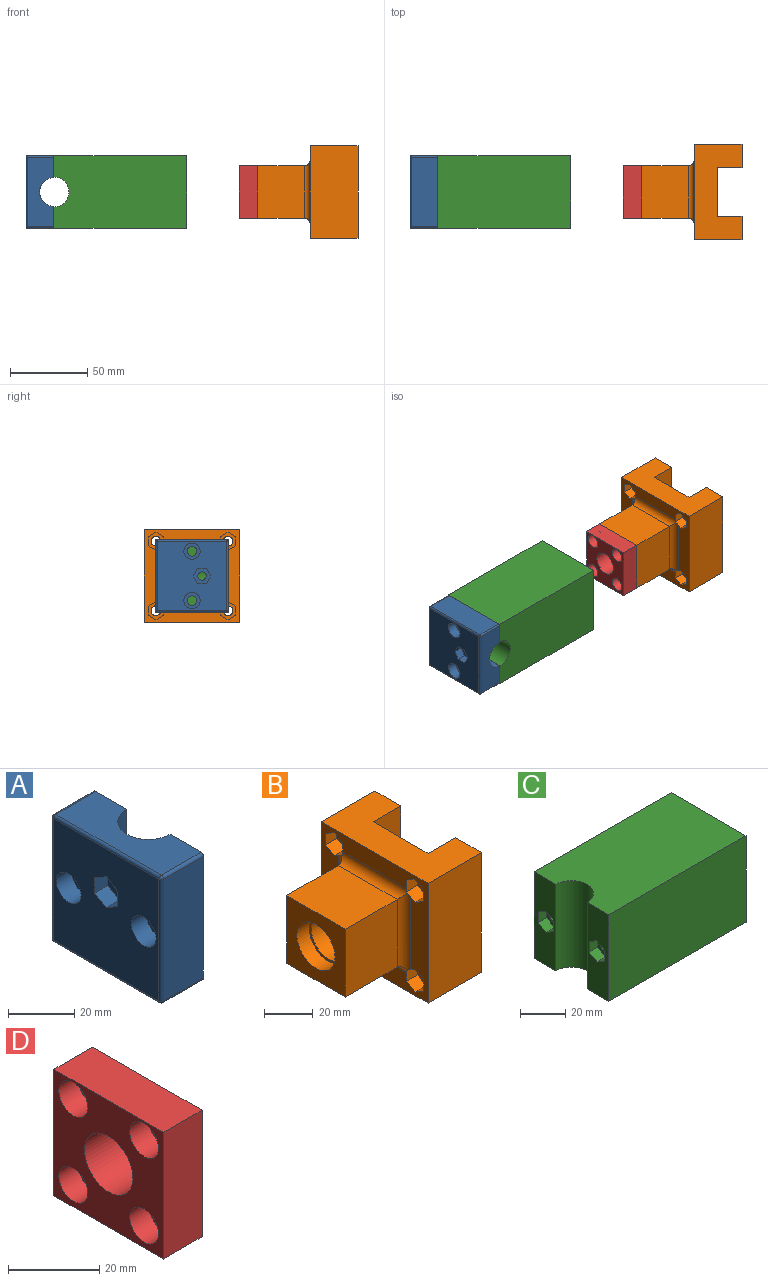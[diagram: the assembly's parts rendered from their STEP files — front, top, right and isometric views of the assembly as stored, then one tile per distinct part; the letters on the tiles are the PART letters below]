
ASSEMBLY  parts=4 mates=9
PART A: 34 faces, bbox 18x47x47 mm
  f0: cylinder r=2.7mm len=5.4mm, axis (-1,0,0), area 57.7mm2, adj f13,f33
  f1: plane 47x14.25mm, normal (1,0,0), area 639.1mm2, adj f7,f10,f11,f12,f13,f16,f22
  f2: cylinder r=5.25mm len=10.5mm, axis (-1,0,0), area 214.4mm2, adj f3,f8
  f3: plane 10.5x10.5mm, normal (-1,0,0), area 56.4mm2, adj f2,f4
  f4: cylinder r=3.1mm len=11.5mm, axis (-1,0,0), area 224mm2, adj f3,f14
  f5: cylinder r=5.25mm len=10.5mm, axis (-1,0,0), area 214.4mm2, adj f6,f8
  f6: plane 10.5x10.5mm, normal (-1,0,0), area 56.4mm2, adj f5,f7
  f7: cylinder r=3.1mm len=11.5mm, axis (-1,0,0), area 224mm2, adj f1,f6
  f8: plane 45x45mm, normal (-1,0,0), area 1766.9mm2, adj f2,f5,f17,f20,f23,f26,f27,f28
  f9: plane 45x17mm, normal (0,1,0), area 765mm2, adj f14,f15,f20,f21
  f10: plane 45x17mm, normal (0,-1,0), area 765mm2, adj f1,f16,f22,f23
  f11: plane 45x17mm, normal (0,0,-1), area 630.6mm2, adj f1,f13,f14,f15,f16,f17
  f12: plane 45x17mm, normal (0,0,1), area 630.6mm2, adj f1,f13,f14,f21,f22,f26
  f13: cylinder r=9.25mm len=47mm, axis (0,0,1), area 1342.7mm2, adj f0,f1,f11,f12,f14
  f14: plane 47x14.25mm, normal (1,0,0), area 639.1mm2, adj f4,f9,f11,f12,f13,f15,f21
  f15: cylinder r=1mm len=17mm, axis (1,0,0), area 26.7mm2, adj f9,f11,f14,f18
  f16: cylinder r=1mm len=17mm, axis (-1,0,0), area 26.7mm2, adj f1,f10,f11,f19
  f17: cylinder r=1mm len=45mm, axis (0,-1,0), area 70.7mm2, adj f8,f11,f18,f19
  f18: sphere r=1mm, area 1.6mm2, adj f15,f17,f20
  f19: sphere r=1mm, area 1.6mm2, adj f16,f17,f23
  f20: cylinder r=1mm len=45mm, axis (0,0,1), area 70.7mm2, adj f8,f9,f18,f24
  f21: cylinder r=1mm len=17mm, axis (-1,0,0), area 26.7mm2, adj f9,f12,f14,f24
  f22: cylinder r=1mm len=17mm, axis (1,0,0), area 26.7mm2, adj f1,f10,f12,f25
  f23: cylinder r=1mm len=45mm, axis (0,0,-1), area 70.7mm2, adj f8,f10,f19,f25
  f24: sphere r=1mm, area 1.6mm2, adj f20,f21,f26
  f25: sphere r=1mm, area 1.6mm2, adj f22,f23,f26
  f26: cylinder r=1mm len=45mm, axis (0,1,0), area 70.7mm2, adj f8,f12,f24,f25
  f27: plane 5.55x4.95mm, normal (0,-0.5,-0.87), area 31.7mm2, adj f8,f28,f32,f33
  f28: plane 5.72x5.55mm, normal (0,-1,0), area 31.7mm2, adj f8,f27,f29,f33
  f29: plane 5.55x4.95mm, normal (0,-0.5,0.87), area 31.7mm2, adj f8,f28,f30,f33
  f30: plane 5.55x4.95mm, normal (0,0.5,0.87), area 31.7mm2, adj f8,f29,f31,f33
  f31: plane 5.72x5.55mm, normal (0,1,0), area 31.7mm2, adj f8,f30,f32,f33
  f32: plane 5.55x4.95mm, normal (0,0.5,-0.87), area 31.7mm2, adj f8,f27,f31,f33
  f33: plane 11.43x9.9mm, normal (-1,0,0), area 62mm2, adj f0,f27,f28,f29,f30,f31,f32
PART B: 55 faces, bbox 64.9x61.8x60 mm
  f0: plane 61.75x60mm, normal (-1,0,0), area 1617.1mm2, adj f5,f6,f7,f8,f15,f16,f17,f18
  f1: plane 60x15mm, normal (1,0,0), area 837.7mm2, adj f3,f5,f6,f8,f9,f11
  f2: plane 60x15mm, normal (1,0,0), area 837.7mm2, adj f4,f5,f6,f7,f10,f12
  f3: cylinder r=3.15mm len=24.38mm, axis (1,0,0), area 482.4mm2, adj f1,f28
  f4: cylinder r=3.15mm len=24.38mm, axis (1,0,0), area 482.4mm2, adj f2,f14
  f5: plane 61.75x30.88mm, normal (0,0,1), area 1402.5mm2, adj f0,f1,f2,f7,f8,f9,f10,f13
  f6: plane 61.75x30.88mm, normal (0,0,-1), area 1402.5mm2, adj f0,f1,f2,f7,f8,f9,f10,f13
  f7: plane 60x30.88mm, normal (0,1,0), area 1852.5mm2, adj f0,f2,f5,f6
  f8: plane 60x30.88mm, normal (0,-1,0), area 1852.5mm2, adj f0,f1,f5,f6
  f9: plane 60x15.88mm, normal (0,1,0), area 952.5mm2, adj f1,f5,f6,f13
  f10: plane 60x15.88mm, normal (0,-1,0), area 952.5mm2, adj f2,f5,f6,f13
  f11: cylinder r=3.15mm len=24.38mm, axis (1,0,0), area 482.4mm2, adj f1,f21
  f12: cylinder r=3.15mm len=24.38mm, axis (1,0,0), area 482.4mm2, adj f2,f35
  f13: plane 60x31.75mm, normal (1,0,0), area 1905mm2, adj f5,f6,f9,f10
  f14: plane 11.55x10mm, normal (-1,0,0), area 55.4mm2, adj f4,f15,f16,f17,f18,f19,f20
  f15: plane 6.5x5mm, normal (0,-0.5,-0.87), area 37.5mm2, adj f0,f14,f16,f20
  f16: plane 6.5x5mm, normal (0,0.5,-0.87), area 37.5mm2, adj f0,f14,f15,f17
  f17: plane 6.75x5.77mm, normal (0,1,0), area 37.6mm2, adj f0,f14,f16,f18,f48
  f18: plane 6.96x5.01mm, normal (0,0.5,0.87), area 38.1mm2, adj f0,f14,f17,f19,f48,f50
  f19: plane 6.5x5mm, normal (0,-0.5,0.87), area 37.5mm2, adj f0,f14,f18,f20
  f20: plane 6.5x5.77mm, normal (0,-1,0), area 37.5mm2, adj f0,f14,f15,f19
  f21: plane 11.55x10mm, normal (-1,0,0), area 55.4mm2, adj f11,f22,f23,f24,f25,f26,f27
  f22: plane 6.5x5mm, normal (0,-0.5,-0.87), area 37.5mm2, adj f0,f21,f23,f27
  f23: plane 6.5x5mm, normal (0,0.5,-0.87), area 37.5mm2, adj f0,f21,f22,f24
  f24: plane 6.5x5.77mm, normal (0,1,0), area 37.5mm2, adj f0,f21,f23,f25
  f25: plane 6.5x5mm, normal (0,0.5,0.87), area 37.5mm2, adj f0,f21,f24,f26
  f26: plane 6.96x5.01mm, normal (0,-0.5,0.87), area 38.1mm2, adj f0,f21,f25,f27,f47,f48
  f27: plane 6.75x5.77mm, normal (0,-1,0), area 37.6mm2, adj f0,f21,f22,f26,f48
  f28: plane 11.55x10mm, normal (-1,0,0), area 55.4mm2, adj f3,f29,f30,f31,f32,f33,f34
  f29: plane 6.5x5mm, normal (0,0.5,0.87), area 37.5mm2, adj f0,f28,f30,f34
  f30: plane 6.5x5mm, normal (0,-0.5,0.87), area 37.5mm2, adj f0,f28,f29,f31
  f31: plane 6.75x5.77mm, normal (0,-1,0), area 37.6mm2, adj f0,f28,f30,f32,f49
  f32: plane 6.96x5.01mm, normal (0,-0.5,-0.87), area 38.1mm2, adj f0,f28,f31,f33,f47,f49
  f33: plane 6.5x5mm, normal (0,0.5,-0.87), area 37.5mm2, adj f0,f28,f32,f34
  f34: plane 6.5x5.77mm, normal (0,1,0), area 37.5mm2, adj f0,f28,f29,f33
  f35: plane 11.55x10mm, normal (-1,0,0), area 55.4mm2, adj f12,f36,f37,f38,f39,f40,f41
  f36: plane 6.5x5mm, normal (0,0.5,0.87), area 37.5mm2, adj f0,f35,f37,f41
  f37: plane 6.5x5mm, normal (0,-0.5,0.87), area 37.5mm2, adj f0,f35,f36,f38
  f38: plane 6.5x5.77mm, normal (0,-1,0), area 37.5mm2, adj f0,f35,f37,f39
  f39: plane 6.5x5mm, normal (0,-0.5,-0.87), area 37.5mm2, adj f0,f35,f38,f40
  f40: plane 6.96x5.01mm, normal (0,0.5,-0.87), area 38.1mm2, adj f0,f35,f39,f41,f49,f50
  f41: plane 6.75x5.77mm, normal (0,1,0), area 37.6mm2, adj f0,f35,f36,f40,f49
  f42: plane 34x30mm, normal (0,1,0), area 1020mm2, adj f43,f45,f46,f50
  f43: plane 34x30mm, normal (0,0,-1), area 1020mm2, adj f42,f44,f46,f49
  f44: plane 34x30mm, normal (0,-1,0), area 1020mm2, adj f43,f45,f46,f47
  f45: plane 34x30mm, normal (0,0,1), area 1020mm2, adj f42,f44,f46,f48
  f46: plane 34x34mm, normal (-1,0,0), area 774.1mm2, adj f42,f43,f44,f45,f52
  f47: cylinder r=4mm len=38.32mm, axis (0,0,-1), area 226.5mm2, adj f0,f26,f32,f44,f48,f49
  f48: cylinder r=4mm len=38.32mm, axis (0,-1,0), area 225.8mm2, adj f0,f17,f18,f26,f27,f45,f47,f50
  f49: cylinder r=4mm len=38.32mm, axis (0,1,0), area 225.8mm2, adj f0,f31,f32,f40,f41,f43,f47,f50
  f50: cylinder r=4mm len=38.32mm, axis (0,0,1), area 226.5mm2, adj f0,f18,f40,f42,f48,f49
  f51: plane 22.05x22.05mm, normal (-1,0,0), area 77.1mm2, adj f52,f54
  f52: cylinder r=11.03mm len=22.05mm, axis (-1,0,0), area 491.8mm2, adj f46,f51
  f53: plane 19.7x19.7mm, normal (-1,0,0), area 304.8mm2, adj f54
  f54: cylinder r=9.85mm len=22.9mm, axis (-1,0,0), area 1417.3mm2, adj f51,f53
PART C: 33 faces, bbox 86x47x47 mm
  f0: plane 47x13.75mm, normal (-1,0,0), area 561.4mm2, adj f12,f13,f14,f15,f26,f27,f28,f29
  f1: plane 47x13.75mm, normal (-1,0,0), area 561.4mm2, adj f4,f5,f6,f7,f9,f10,f11,f12
  f2: plane 6.2x6.2mm, normal (-1,0,0), area 30.2mm2, adj f3
  f3: cylinder r=3.1mm len=7.72mm, axis (-1,0,0), area 150.4mm2, adj f2,f8
  f4: plane 5.3x4.95mm, normal (0,0.5,-0.87), area 30.3mm2, adj f1,f5,f7,f8
  f5: plane 5.72x5.3mm, normal (0,1,0), area 30.3mm2, adj f1,f4,f6,f8
  f6: plane 5.3x4.95mm, normal (0,0.5,0.87), area 30.3mm2, adj f1,f5,f8,f9
  f7: plane 5.3x4.95mm, normal (0,-0.5,-0.87), area 30.3mm2, adj f1,f4,f8,f10
  f8: plane 11.43x9.9mm, normal (-1,0,0), area 54.7mm2, adj f3,f4,f5,f6,f7,f9,f10
  f9: plane 5.3x4.95mm, normal (0,-0.5,0.87), area 30.3mm2, adj f1,f6,f8,f10
  f10: plane 5.72x5.3mm, normal (0,-1,0), area 30.3mm2, adj f1,f7,f8,f9
  f11: plane 86x47mm, normal (0,1,0), area 4042mm2, adj f1,f12,f14,f16
  f12: plane 86x47mm, normal (0,0,-1), area 3892.7mm2, adj f0,f1,f11,f13,f15,f16
  f13: plane 86x47mm, normal (0,-1,0), area 4042mm2, adj f0,f12,f14,f16
  f14: plane 86x47mm, normal (0,0,1), area 3892.7mm2, adj f0,f1,f11,f13,f15,f16
  f15: cylinder r=9.75mm len=47mm, axis (0,0,1), area 1439.6mm2, adj f0,f1,f12,f14
  f16: plane 47x47mm, normal (1,0,0), area 1011.8mm2, adj f11,f12,f13,f14,f17,f18,f19,f20
  f17: plane 34.6x28mm, normal (0,1,0), area 968.8mm2, adj f16,f18,f20,f23
  f18: plane 34.6x28mm, normal (0,0,-1), area 968.8mm2, adj f16,f17,f19,f23
  f19: plane 34.6x28mm, normal (0,-1,0), area 968.8mm2, adj f16,f18,f20,f23
  f20: plane 34.6x28mm, normal (0,0,1), area 968.8mm2, adj f16,f17,f19,f23
  f21: plane 8x8mm, normal (1,0,0), area 50.3mm2, adj f22
  f22: cylinder r=4mm len=20mm, axis (1,0,0), area 502.7mm2, adj f21,f23
  f23: plane 34.6x34.6mm, normal (1,0,0), area 1146.9mm2, adj f17,f18,f19,f20,f22
  f24: plane 6.2x6.2mm, normal (-1,0,0), area 30.2mm2, adj f25
  f25: cylinder r=3.1mm len=7.72mm, axis (-1,0,0), area 150.4mm2, adj f24,f30
  f26: plane 5.3x4.95mm, normal (0,-0.5,-0.87), area 30.3mm2, adj f0,f27,f29,f30
  f27: plane 5.3x4.95mm, normal (0,0.5,-0.87), area 30.3mm2, adj f0,f26,f28,f30
  f28: plane 5.72x5.3mm, normal (0,1,0), area 30.3mm2, adj f0,f27,f30,f31
  f29: plane 5.72x5.3mm, normal (0,-1,0), area 30.3mm2, adj f0,f26,f30,f32
  f30: plane 11.43x9.9mm, normal (-1,0,0), area 54.7mm2, adj f25,f26,f27,f28,f29,f31,f32
  f31: plane 5.3x4.95mm, normal (0,0.5,0.87), area 30.3mm2, adj f0,f28,f30,f32
  f32: plane 5.3x4.95mm, normal (0,-0.5,0.87), area 30.3mm2, adj f0,f29,f30,f31
PART D: 19 faces, bbox 12x34x34 mm
  f0: cylinder r=2.6mm len=6mm, axis (1,0,0), area 98mm2, adj f10,f18
  f1: cylinder r=2.6mm len=6mm, axis (1,0,0), area 98mm2, adj f10,f16
  f2: cylinder r=2.6mm len=6mm, axis (1,0,0), area 98mm2, adj f10,f14
  f3: cylinder r=2.6mm len=6mm, axis (1,0,0), area 98mm2, adj f10,f12
  f4: plane 34x12mm, normal (0,0,1), area 408mm2, adj f5,f8,f9,f10
  f5: plane 34x12mm, normal (0,1,0), area 408mm2, adj f4,f6,f9,f10
  f6: plane 34x12mm, normal (0,0,-1), area 408mm2, adj f5,f8,f9,f10
  f7: cylinder r=7.5mm len=15mm, axis (1,0,0), area 565.5mm2, adj f9,f10
  f8: plane 34x12mm, normal (0,-1,0), area 408mm2, adj f4,f6,f9,f10
  f9: plane 34x34mm, normal (-1,0,0), area 730.4mm2, adj f4,f5,f6,f7,f8,f11,f13,f15
  f10: plane 34x34mm, normal (1,0,0), area 894.3mm2, adj f0,f1,f2,f3,f4,f5,f6,f7
  f11: cylinder r=4.45mm len=8.9mm, axis (-1,0,0), area 167.8mm2, adj f9,f12
  f12: plane 8.9x8.9mm, normal (-1,0,0), area 41mm2, adj f3,f11
  f13: cylinder r=4.45mm len=8.9mm, axis (-1,0,0), area 167.8mm2, adj f9,f14
  f14: plane 8.9x8.9mm, normal (-1,0,0), area 41mm2, adj f2,f13
  f15: cylinder r=4.45mm len=8.9mm, axis (-1,0,0), area 167.8mm2, adj f9,f16
  f16: plane 8.9x8.9mm, normal (-1,0,0), area 41mm2, adj f1,f15
  f17: cylinder r=4.45mm len=8.9mm, axis (-1,0,0), area 167.8mm2, adj f9,f18
  f18: plane 8.9x8.9mm, normal (-1,0,0), area 41mm2, adj f0,f17
PLACE A rot(axis=(1,0,0),90deg) t=(-39.22,0.63,-40.98)mm
PLACE B t=(1.56,10.12,-104.29)mm fixed
PLACE C rot(axis=(1,0,0),90deg) t=(-39.22,0.63,-40.98)mm
PLACE D t=(24.88,14.4,-97.94)mm
MATE cylindrical D.f7 <-> C.f22  axis (-1,0,0) through (-75.31,10.12,-74.29)mm
MATE cylindrical C.f25 <-> A.f5  axis (-1,0,0) through (-190.25,10.12,-90.29)mm
MATE cylindrical C.f3 <-> A.f2  axis (-1,0,0) through (-190.25,10.12,-58.29)mm
MATE planar D.f6 <-> B.f43  axis (0,0,-1) through (-69.31,10.12,-91.29)mm
MATE planar D.f10 <-> B.f46  axis (1,0,0) through (-63.31,-6.88,-74.29)mm
MATE planar A.f1 <-> C.f0  axis (1,0,0) through (-195.55,33.62,-83.54)mm
MATE parallel B.f44 <-> C.f18  axis (0,-1,0) through (-48.31,-6.88,-74.29)mm
MATE parallel C.f14 <-> A.f12  axis (0,-1,0) through (-151.06,-13.38,-74.29)mm
MATE planar D.f8 <-> B.f44  axis (0,-1,0) through (-69.31,-6.88,-74.29)mm
